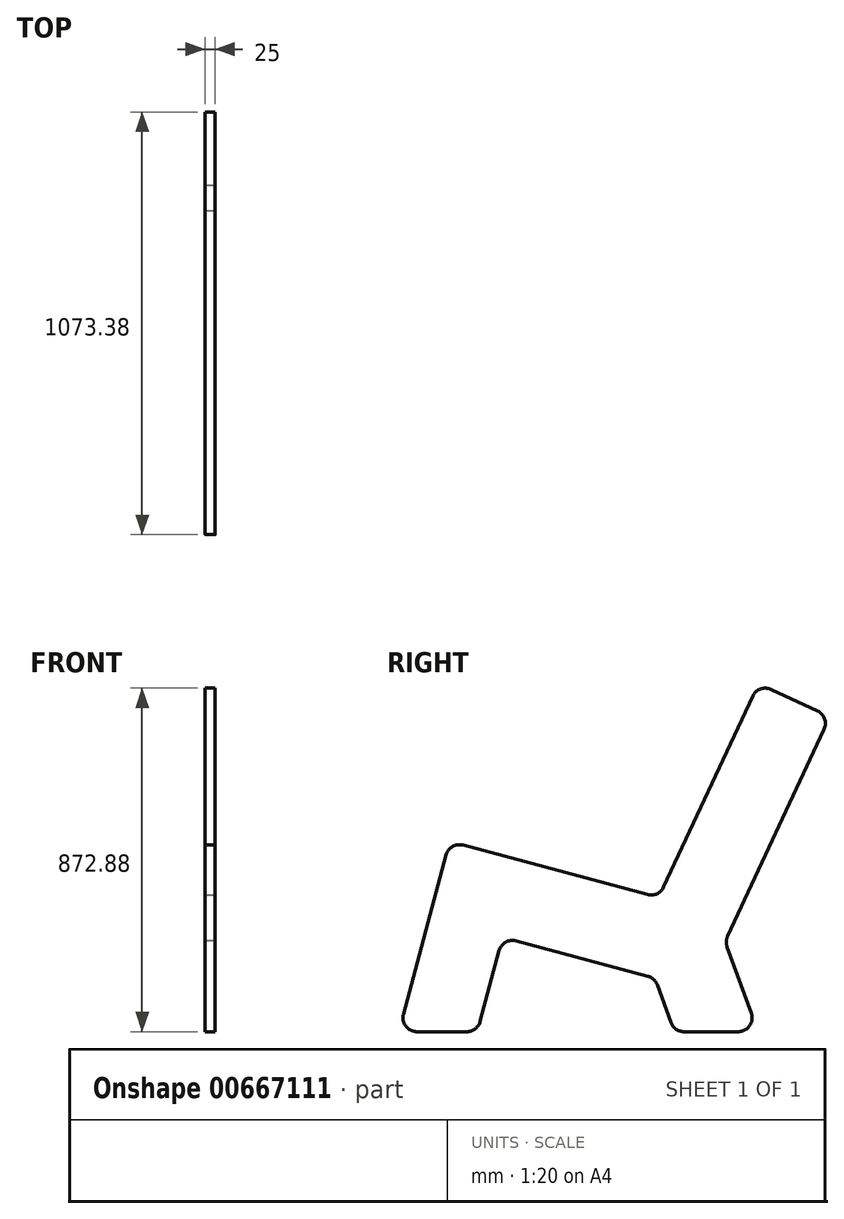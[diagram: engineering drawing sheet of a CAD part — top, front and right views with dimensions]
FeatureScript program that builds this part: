
annotation { "Feature Type Name" : "Feature", "Feature Type Description" : "" }
export const myFeature = defineFeature(function(context is Context, id is Id, definition is map)
    precondition{}
    {
        {
            var Q0;
            Q0=qCreatedBy(makeId("Right.planeOp"),FACE);
            var sketch = newSketch(context, id + "F0", { "sketchPlane" : qUnion([Q0])});
            skLineSegment(sketch, "E0", {"start": v(0, 0) * mm, "end": v(200, 0) * mm});
            skLineSegment(sketch, "E1", {"start": v(0, 0) * mm, "end": v(129.4, 482.96) * mm});
            skLineSegment(sketch, "E2", {"start": v(200, 0) * mm, "end": v(264.25, 239.78) * mm});
            skLineSegment(sketch, "E3", {"start": v(129.4, 482.96) * mm, "end": v(660.67, 340.61) * mm});
            skLineSegment(sketch, "E4", {"start": v(660.67, 340.61) * mm, "end": v(914.24, 884.4) * mm});
            skLineSegment(sketch, "E5", {"start": v(914.24, 884.4) * mm, "end": v(1095.5, 799.87) * mm});
            skLineSegment(sketch, "E6", {"start": v(700, 0) * mm, "end": v(912.84, 0) * mm});
            skLineSegment(sketch, "E7", {"start": v(264.25, 239.78) * mm, "end": v(650.39, 136.31) * mm});
            skLineSegment(sketch, "E8", {"start": v(650.39, 136.31) * mm, "end": v(700, 0) * mm});
            skLineSegment(sketch, "E9", {"start": v(1095.5, 799.87) * mm, "end": v(829.4, 229.23) * mm});
            skLineSegment(sketch, "E10", {"start": v(912.84, 0) * mm, "end": v(829.4, 229.23) * mm});
            skSolve(sketch);
        }
        {
            var Q0;
            Q0 = qSketchRegion(id + "F0", true);
            extrude(context, id + "F1", {"entities" : qUnion([Q0]), "depth" : 25 * mm, "offsetDistance" : 25 * mm});
        }
        {
            var Q0;
            Q0=makeQuery(id+"F1.opExtrude","SWEPT_EDGE",EDGE,{"disambiguationData":[OSD([sQuery(id+"F0.wireOp",EDGE,"E0"),sQuery(id+"F0.wireOp",EDGE,"E1")])]});
            var Q1;
            Q1=makeQuery(id+"F1.opExtrude","SWEPT_EDGE",EDGE,{"disambiguationData":[OSD([sQuery(id+"F0.wireOp",EDGE,"E1"),sQuery(id+"F0.wireOp",EDGE,"E3")])]});
            var Q2;
            Q2=makeQuery(id+"F1.opExtrude","SWEPT_EDGE",EDGE,{"disambiguationData":[OSD([sQuery(id+"F0.wireOp",EDGE,"E3"),sQuery(id+"F0.wireOp",EDGE,"E4")])]});
            var Q3;
            Q3=makeQuery(id+"F1.opExtrude","SWEPT_EDGE",EDGE,{"disambiguationData":[OSD([sQuery(id+"F0.wireOp",EDGE,"E4"),sQuery(id+"F0.wireOp",EDGE,"E5")])]});
            var Q4;
            Q4=makeQuery(id+"F1.opExtrude","SWEPT_EDGE",EDGE,{"disambiguationData":[OSD([sQuery(id+"F0.wireOp",EDGE,"E5"),sQuery(id+"F0.wireOp",EDGE,"E9")])]});
            var Q5;
            Q5=makeQuery(id+"F1.opExtrude","SWEPT_EDGE",EDGE,{"disambiguationData":[OSD([sQuery(id+"F0.wireOp",EDGE,"E9"),sQuery(id+"F0.wireOp",EDGE,"E10")])]});
            var Q6;
            Q6=makeQuery(id+"F1.opExtrude","SWEPT_EDGE",EDGE,{"disambiguationData":[OSD([sQuery(id+"F0.wireOp",EDGE,"E6"),sQuery(id+"F0.wireOp",EDGE,"E10")])]});
            var Q7;
            Q7=makeQuery(id+"F1.opExtrude","SWEPT_EDGE",EDGE,{"disambiguationData":[OSD([sQuery(id+"F0.wireOp",EDGE,"E6"),sQuery(id+"F0.wireOp",EDGE,"E8")])]});
            var Q8;
            Q8=makeQuery(id+"F1.opExtrude","SWEPT_EDGE",EDGE,{"disambiguationData":[OSD([sQuery(id+"F0.wireOp",EDGE,"E7"),sQuery(id+"F0.wireOp",EDGE,"E8")])]});
            var Q9;
            Q9=makeQuery(id+"F1.opExtrude","SWEPT_EDGE",EDGE,{"disambiguationData":[OSD([sQuery(id+"F0.wireOp",EDGE,"E0"),sQuery(id+"F0.wireOp",EDGE,"E2")])]});
            var Q10;
            Q10=makeQuery(id+"F1.opExtrude","SWEPT_EDGE",EDGE,{"disambiguationData":[OSD([sQuery(id+"F0.wireOp",EDGE,"E2"),sQuery(id+"F0.wireOp",EDGE,"E7")])]});
            fillet(context, id + "F2", {"entities" : qUnion([Q0, Q1, Q2, Q3, Q4, Q5, Q6, Q7, Q8, Q9, Q10]), "radius" : 35 * mm, "tangentPropagation" : true, "allowEdgeOverflow" : false});
        }
    });
